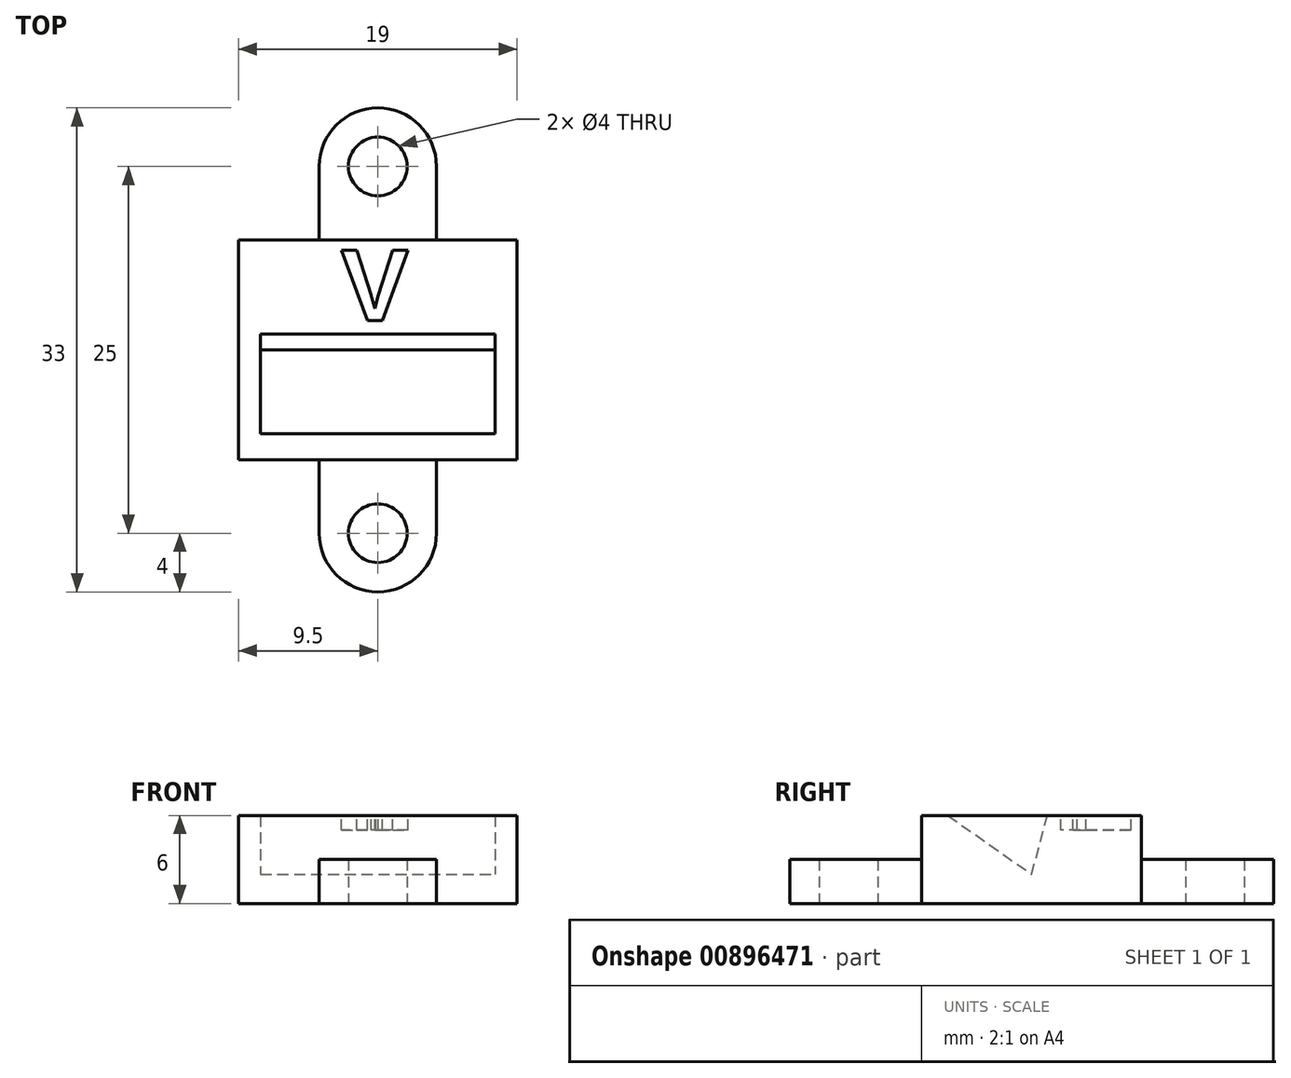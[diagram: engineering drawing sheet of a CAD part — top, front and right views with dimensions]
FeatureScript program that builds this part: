
annotation { "Feature Type Name" : "Feature", "Feature Type Description" : "" }
export const myFeature = defineFeature(function(context is Context, id is Id, definition is map)
    precondition{}
    {
        {
            var Q0;
            Q0=qCreatedBy(makeId("Top.planeOp"),FACE);
            var sketch = newSketch(context, id + "F0", { "sketchPlane" : qUnion([Q0])});
            skLineSegment(sketch, "E0.bottom", {"start": v(-9.5, 7.5) * mm, "end": v(9.5, 7.5) * mm});
            skLineSegment(sketch, "E0.top", {"start": v(-9.5, -7.5) * mm, "end": v(9.5, -7.5) * mm});
            skLineSegment(sketch, "E0.left", {"start": v(-9.5, 7.5) * mm, "end": v(-9.5, -7.5) * mm});
            skLineSegment(sketch, "E0.right", {"start": v(9.5, 7.5) * mm, "end": v(9.5, -7.5) * mm});
            skPoint(sketch, "E1", {"position": v(0, 7.5) * mm});
            skPoint(sketch, "E2", {"position": v(0, -7.5) * mm});
            skPoint(sketch, "E3", {"position": v(9.5, 0) * mm});
            skPoint(sketch, "E4", {"position": v(-9.5, 0) * mm});
            skSolve(sketch);
        }
        {
            var Q0;
            Q0=qSketchRegion(id+"F0",true);
            extrude(context, id + "F1", {"entities" : qUnion([Q0]), "depth" : 6 * mm, "offsetDistance" : 25 * mm});
        }
        {
            var Q0;
            Q0=qCreatedBy(makeId("Right.planeOp"),FACE);
            var sketch = newSketch(context, id + "F2", { "sketchPlane" : qUnion([Q0])});
            skLineSegment(sketch, "E5", {"start": v(-5.71, 6) * mm, "end": v(0, 2) * mm});
            skLineSegment(sketch, "E6", {"start": v(0, 2) * mm, "end": v(1.07, 6) * mm});
            skLineSegment(sketch, "E7", {"start": v(1.07, 6) * mm, "end": v(-5.71, 6) * mm});
            skSolve(sketch);
        }
        {
            var Q0;
            Q0=qSketchRegion(id+"F2",true);
            extrude(context, id + "F3", {"entities" : qUnion([Q0]), "operationType" : NewBodyOperationType.REMOVE, "oppositeDirection" : true, "depth" : 16 * mm, "offsetDistance" : 25 * mm, "symmetric" : true});
        }
        {
            var Q0;
            Q0=qCreatedBy(makeId("Top.planeOp"),FACE);
            var sketch = newSketch(context, id + "F4", { "sketchPlane" : qUnion([Q0])});
            skLineSegment(sketch, "E8.bottom", {"start": v(-4, 7.5) * mm, "end": v(4, 7.5) * mm});
            skLineSegment(sketch, "E8.left", {"start": v(-4, 7.5) * mm, "end": v(-4, 12.5) * mm});
            skLineSegment(sketch, "E8.right", {"start": v(4, 7.5) * mm, "end": v(4, 12.5) * mm});
            skPoint(sketch, "E9", {"position": v(0, 12.5) * mm});
            skArc(sketch, "E10", {"start": v(-4, 12.5) * mm, "mid": v(0, 16.5) * mm, "end": v(4, 12.5) * mm});
            skCircle(sketch, "E11", {"center": v(0, 12.5) * mm, "radius": 2 * mm});
            skPoint(sketch, "E12", {"position": v(0, 7.5) * mm});
            skLineSegment(sketch, "E13.MirrorCS", {"start": v(-4, -7.5) * mm, "end": v(-4, -12.5) * mm});
            skArc(sketch, "E14.MirrorCS", {"start": v(-4, -12.5) * mm, "mid": v(0, -16.5) * mm, "end": v(4, -12.5) * mm});
            skCircle(sketch, "E15.MirrorC", {"center": v(0, -12.5) * mm, "radius": 2 * mm});
            skLineSegment(sketch, "E16.MirrorCS", {"start": v(4, -7.5) * mm, "end": v(4, -12.5) * mm});
            skLineSegment(sketch, "E17.MirrorCS", {"start": v(-4, -7.5) * mm, "end": v(4, -7.5) * mm});
            skSolve(sketch);
        }
        {
            var Q0;
            Q0=qSketchRegion(id+"F4",true);
            extrude(context, id + "F5", {"entities" : qUnion([Q0]), "operationType" : NewBodyOperationType.ADD, "depth" : 3 * mm, "offsetDistance" : 25 * mm});
        }
        {
            var Q0;
            Q0=makeQuery(id+"F1.opExtrude","CAP_FACE",FACE,{"disambiguationData":[OSD([sQuery(id+"F0.wireOp",EDGE,"E0.bottom"),sQuery(id+"F0.wireOp",EDGE,"E0.top"),sQuery(id+"F0.wireOp",EDGE,"E0.left"),sQuery(id+"F0.wireOp",EDGE,"E0.right")])],"isStart":false});
            var sketch = newSketch(context, id + "F6", { "sketchPlane" : qUnion([Q0])});
            skText(sketch, "E18", { "text": "V", "fontName": "Arimo-Bold.ttf"});
            const initialGuessF6  = {"E18": [-0.00253, 0.002, 1, 0, 0.005]};
            skSetInitialGuess(sketch, initialGuessF6);
            skSolve(sketch);
        }
        {
            var Q0;
            Q0 = qSketchRegion(id + "F6", true);
            extrude(context, id + "F7", {"entities" : qUnion([Q0]), "operationType" : NewBodyOperationType.REMOVE, "oppositeDirection" : true, "depth" : 1 * mm, "offsetDistance" : 25 * mm});
        }
    });
